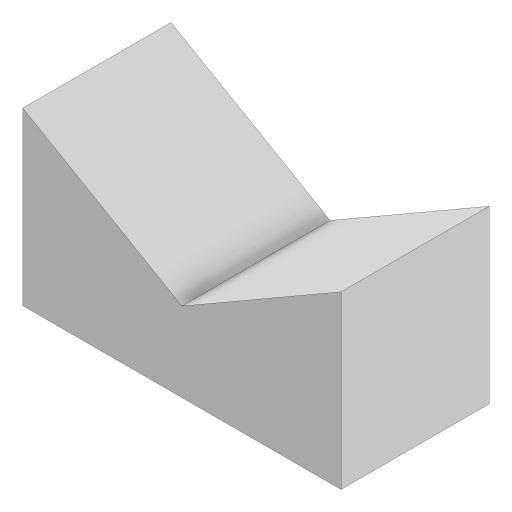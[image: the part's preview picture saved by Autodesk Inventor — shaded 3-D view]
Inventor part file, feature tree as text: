
AUTODESK INVENTOR PART (.ipt)
format: ipt  version: 2023.3 (Build 273359000, 359)  size: 114,176 bytes
history: native  units: mm
features: extrude x2, sketch x2
ambient origin geometry x8: Origin, YZ Plane, XZ Plane, XY Plane, X Axis, Y Axis, Z Axis, Center Point
bodies: Solid1 (feature_tree)
feature tree (4):
  extrude  "Extrusion1"  Depth=5.8mm
  extrude  "Extrusion2"  Depth=2.7mm TaperAngle=0.0deg
  sketch  "Sketch1"  dims[d0=5.5mm d1=5.8mm]
  sketch  "Sketch2"  dims[d2=6.121mm d3=2.7mm d4=0.0mm d5=1.0mm d6=1.0mm d7=2.0mm d8=1.5mm d9=0.0mm]
